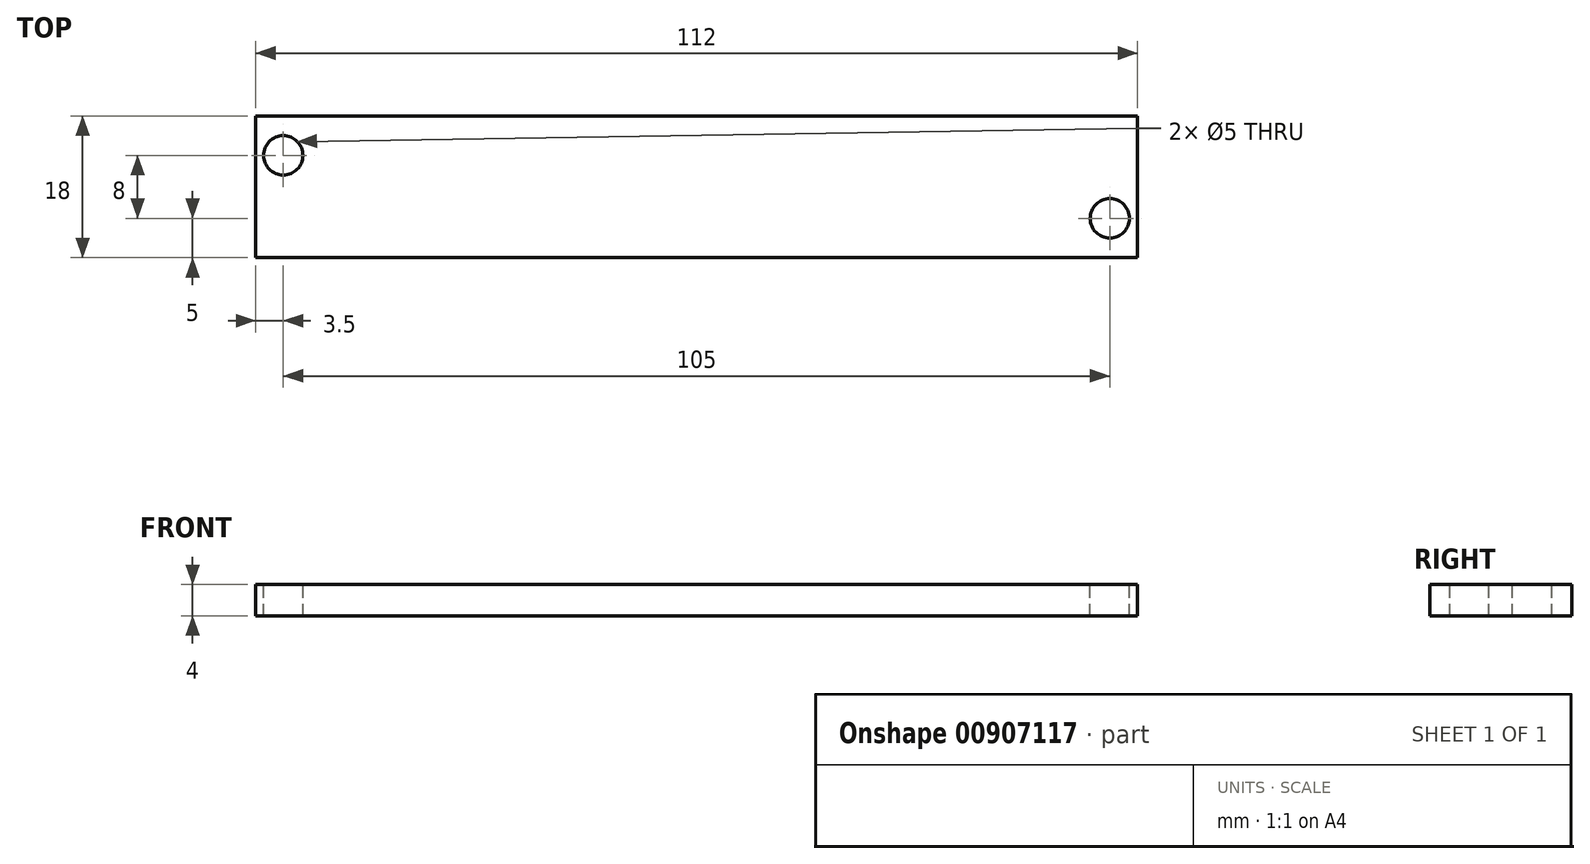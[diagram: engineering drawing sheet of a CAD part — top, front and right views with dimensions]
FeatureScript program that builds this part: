
annotation { "Feature Type Name" : "Feature", "Feature Type Description" : "" }
export const myFeature = defineFeature(function(context is Context, id is Id, definition is map)
    precondition{}
    {
        {
            var Q0;
            Q0=qCreatedBy(makeId("Top.planeOp"),FACE);
            var sketch = newSketch(context, id + "F0", { "sketchPlane" : qUnion([Q0])});
            skLineSegment(sketch, "E0.bottom", {"start": v(56, 9) * mm, "end": v(-56, 9) * mm});
            skLineSegment(sketch, "E0.top", {"start": v(56, -9) * mm, "end": v(-56, -9) * mm});
            skLineSegment(sketch, "E0.left", {"start": v(56, 9) * mm, "end": v(56, -9) * mm});
            skLineSegment(sketch, "E0.right", {"start": v(-56, 9) * mm, "end": v(-56, -9) * mm});
            skPoint(sketch, "E0.middle", {"position": v(0, 0) * mm});
            skSolve(sketch);
        }
        {
            var Q0;
            Q0=makeQuery(id+"F0.imprint","IMPRINT",FACE,{"disambiguationData":[TD([[makeQuery(id+"F0.imprint","IMPRINT",EDGE,{"derivedFrom":sQuery(id+"F0.wireOp",EDGE,"E0.bottom")}),1.0]])]});
            extrude(context, id + "F1", {"entities" : qUnion([Q0]), "depth" : 4 * mm, "offsetDistance" : 25 * mm});
        }
        {
            var Q0;
            Q0=makeQuery(id+"F1.opExtrude","CAP_FACE",FACE,{"disambiguationData":[OSD([sQuery(id+"F0.wireOp",EDGE,"E0.bottom"),sQuery(id+"F0.wireOp",EDGE,"E0.top"),sQuery(id+"F0.wireOp",EDGE,"E0.left"),sQuery(id+"F0.wireOp",EDGE,"E0.right")])],"isStart":false});
            var sketch = newSketch(context, id + "F2", { "sketchPlane" : qUnion([Q0])});
            skCircle(sketch, "E1", {"center": v(-52.5, 4) * mm, "radius": 2.5 * mm});
            skCircle(sketch, "E2.1.0", {"center": v(52.5, -4) * mm, "radius": 2.5 * mm});
            skPoint(sketch, "E2.center", {"position": v(0, 0) * mm});
            skSolve(sketch);
        }
        {
            var Q0;
            Q0=makeQuery(id+"F2.imprint","IMPRINT",FACE,{"disambiguationData":[TD([[makeQuery(id+"F2.imprint","IMPRINT",EDGE,{"derivedFrom":sQuery(id+"F2.wireOp",EDGE,"E1")}),1.0]])]});
            var Q1;
            Q1=makeQuery(id+"F2.imprint","IMPRINT",FACE,{"disambiguationData":[TD([[makeQuery(id+"F2.imprint","IMPRINT",EDGE,{"derivedFrom":sQuery(id+"F2.wireOp",EDGE,"E2.1.0")}),1.0]])]});
            extrude(context, id + "F3", {"entities" : qUnion([Q0, Q1]), "operationType" : NewBodyOperationType.REMOVE, "endBound" : BoundingType.UP_TO_NEXT, "oppositeDirection" : true, "depth" : 25 * mm, "offsetDistance" : 25 * mm});
        }
    });
